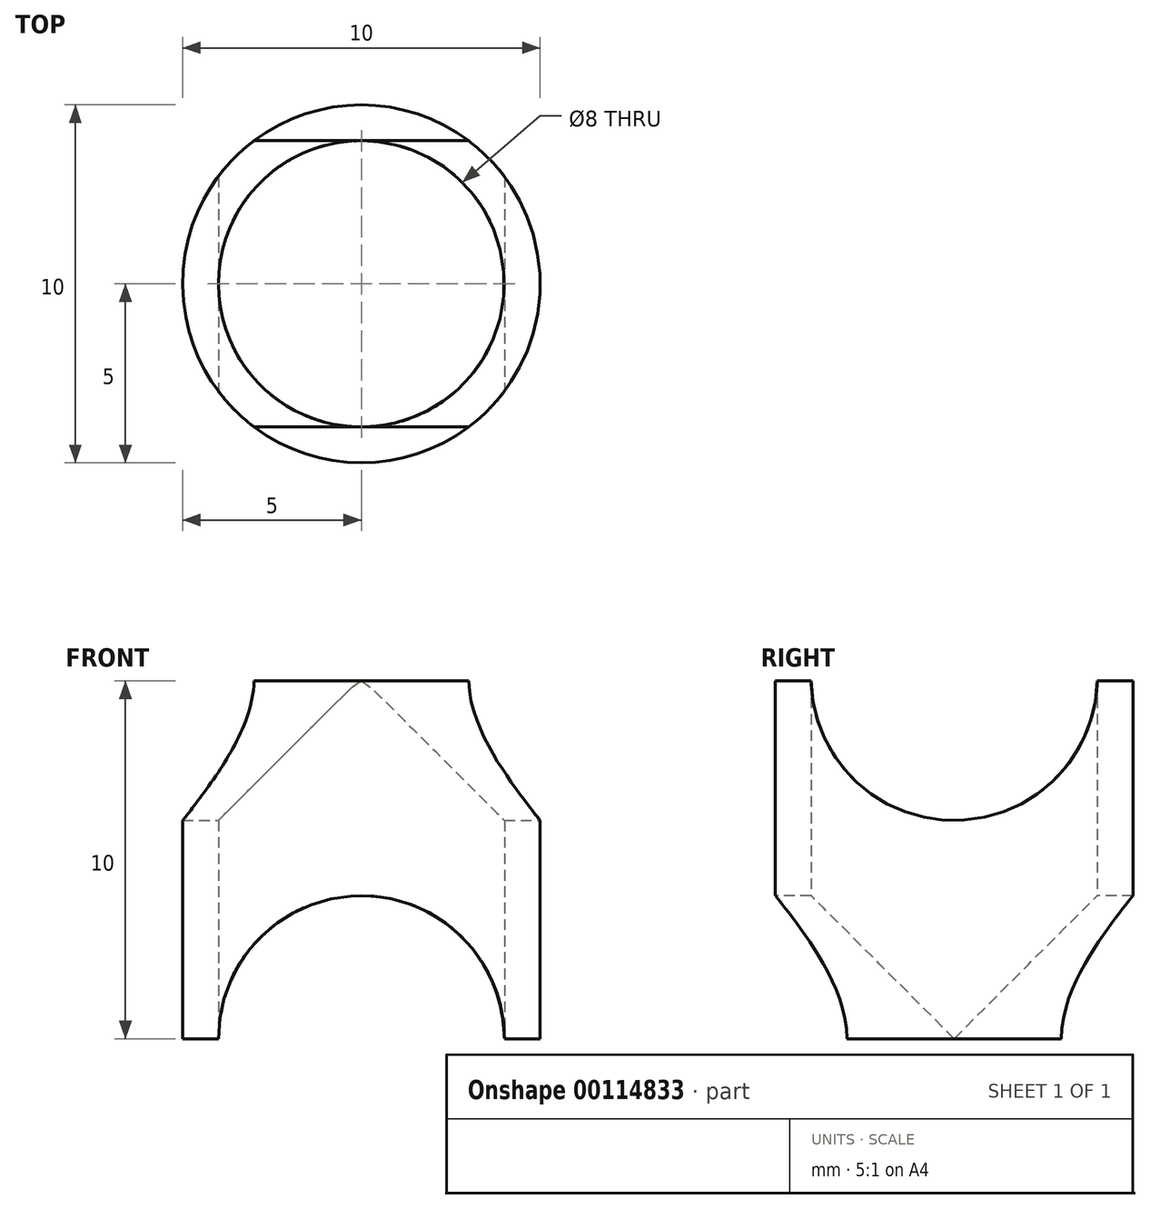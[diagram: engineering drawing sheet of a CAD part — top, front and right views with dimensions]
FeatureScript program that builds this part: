
annotation { "Feature Type Name" : "Feature", "Feature Type Description" : "" }
export const myFeature = defineFeature(function(context is Context, id is Id, definition is map)
    precondition{}
    {
        {
            var Q0;
            Q0=qCreatedBy(makeId("Top.planeOp"),FACE);
            var sketch = newSketch(context, id + "F0", { "sketchPlane" : qUnion([Q0])});
            skCircle(sketch, "E0", {"center": v(0, 0) * mm, "radius": 5 * mm});
            skSolve(sketch);
        }
        {
            var Q0;
            Q0 = qSketchRegion(id + "F0", true);
            extrude(context, id + "F1", {"entities" : qUnion([Q0]), "depth" : 10 * mm});
        }
        {
            var Q0;
            Q0=qCreatedBy(makeId("Front.planeOp"),FACE);
            var sketch = newSketch(context, id + "F2", { "sketchPlane" : qUnion([Q0])});
            skArc(sketch, "E1", {"start": v(-4, 0) * mm, "mid": v(0, 4) * mm, "end": v(4, 0) * mm});
            skLineSegment(sketch, "E2", {"start": v(-4, 0) * mm, "end": v(4, 0) * mm});
            skSolve(sketch);
        }
        {
            var Q0;
            Q0 = qSketchRegion(id + "F2", true);
            extrude(context, id + "F3", {"entities" : qUnion([Q0]), "operationType" : NewBodyOperationType.REMOVE, "endBound" : BoundingType.THROUGH_ALL, "oppositeDirection" : true, "depth" : 25 * mm, "hasSecondDirection" : true, "secondDirectionBound" : SecondDirectionBoundingType.THROUGH_ALL, "secondDirectionOppositeDirection" : false, "secondDirectionDepth" : 25 * mm});
        }
        {
            var Q0;
            Q0=qCreatedBy(makeId("Right.planeOp"),FACE);
            var sketch = newSketch(context, id + "F4", { "sketchPlane" : qUnion([Q0])});
            skArc(sketch, "E3", {"start": v(4, 10) * mm, "mid": v(0, 6.1) * mm, "end": v(-4, 10) * mm});
            skLineSegment(sketch, "E4", {"start": v(4, 10) * mm, "end": v(-4, 10) * mm});
            skSolve(sketch);
        }
        {
            var Q0;
            Q0 = qSketchRegion(id + "F4", true);
            extrude(context, id + "F5", {"entities" : qUnion([Q0]), "operationType" : NewBodyOperationType.REMOVE, "endBound" : BoundingType.THROUGH_ALL, "oppositeDirection" : true, "depth" : 25 * mm, "hasSecondDirection" : true, "secondDirectionBound" : SecondDirectionBoundingType.THROUGH_ALL, "secondDirectionOppositeDirection" : false, "secondDirectionDepth" : 25 * mm});
        }
        {
            var Q0;
            Q0=qCreatedBy(makeId("Top.planeOp"),FACE);
            var sketch = newSketch(context, id + "F6", { "sketchPlane" : qUnion([Q0])});
            skCircle(sketch, "E5", {"center": v(0, 0) * mm, "radius": 4 * mm});
            skSolve(sketch);
        }
        {
            var Q0;
            Q0 = qSketchRegion(id + "F6", true);
            extrude(context, id + "F7", {"entities" : qUnion([Q0]), "operationType" : NewBodyOperationType.REMOVE, "endBound" : BoundingType.THROUGH_ALL, "depth" : 25 * mm});
        }
    });
